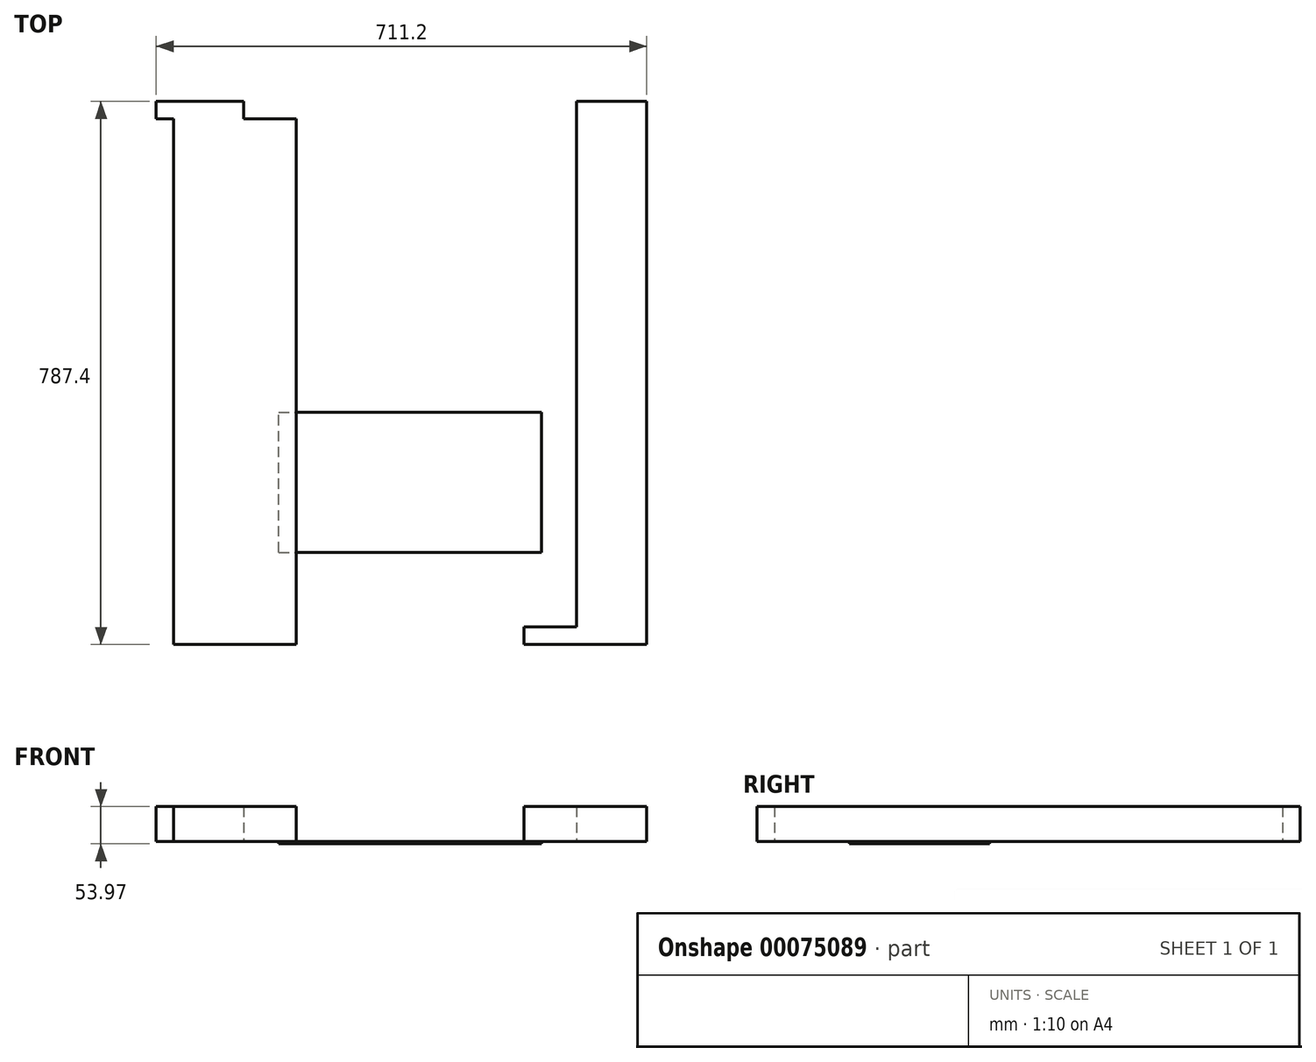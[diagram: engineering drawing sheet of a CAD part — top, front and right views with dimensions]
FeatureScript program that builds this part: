
annotation { "Feature Type Name" : "Feature", "Feature Type Description" : "" }
export const myFeature = defineFeature(function(context is Context, id is Id, definition is map)
    precondition{}
    {
        {
            var Q0;
            Q0=qCreatedBy(makeId("Top.planeOp"),FACE);
            var sketch = newSketch(context, id + "F0", { "sketchPlane" : qUnion([Q0])});
            skLineSegment(sketch, "E0.right", {"start": v(-494.41, 506.03) * mm, "end": v(-494.41, -281.37) * mm});
            skLineSegment(sketch, "E1.right", {"start": v(-596.01, 506.03) * mm, "end": v(-596.01, -281.37) * mm});
            skLineSegment(sketch, "E2.bottom", {"start": v(-621.41, 506.03) * mm, "end": v(115.19, 506.03) * mm});
            skLineSegment(sketch, "E2.top", {"start": v(-621.41, -281.37) * mm, "end": v(115.19, -281.37) * mm});
            skLineSegment(sketch, "E3.right", {"start": v(89.79, 506.03) * mm, "end": v(89.79, -281.37) * mm});
            skLineSegment(sketch, "E4.left", {"start": v(-11.81, 506.03) * mm, "end": v(-11.81, -281.37) * mm});
            skLineSegment(sketch, "E4.right", {"start": v(13.59, 506.03) * mm, "end": v(13.59, -281.37) * mm});
            skLineSegment(sketch, "E5.bottom", {"start": v(-621.41, -281.37) * mm, "end": v(-418.21, -281.37) * mm});
            skLineSegment(sketch, "E6.bottom", {"start": v(115.19, -281.37) * mm, "end": v(-88.01, -281.37) * mm});
            skLineSegment(sketch, "E5.top", {"start": v(-621.41, -255.97) * mm, "end": v(-418.21, -255.97) * mm});
            skLineSegment(sketch, "E6.top", {"start": v(115.19, -255.97) * mm, "end": v(-88.01, -255.97) * mm});
            skLineSegment(sketch, "E0.left", {"start": v(-519.81, 506.03) * mm, "end": v(-519.81, -281.37) * mm});
            skLineSegment(sketch, "E6.left", {"start": v(115.19, -281.37) * mm, "end": v(115.19, -255.97) * mm});
            skLineSegment(sketch, "E1.top", {"start": v(-621.41, -281.37) * mm, "end": v(-596.01, -281.37) * mm});
            skLineSegment(sketch, "E3.bottom", {"start": v(115.19, 506.03) * mm, "end": v(89.79, 506.03) * mm});
            skLineSegment(sketch, "E3.top", {"start": v(115.19, -281.37) * mm, "end": v(89.79, -281.37) * mm});
            skLineSegment(sketch, "E4.bottom", {"start": v(-11.81, 506.03) * mm, "end": v(13.59, 506.03) * mm});
            skLineSegment(sketch, "E4.top", {"start": v(-11.81, -281.37) * mm, "end": v(13.59, -281.37) * mm});
            skLineSegment(sketch, "E1.bottom", {"start": v(-621.41, 506.03) * mm, "end": v(-596.01, 506.03) * mm});
            skLineSegment(sketch, "E6.right", {"start": v(-88.01, -281.37) * mm, "end": v(-88.01, -255.97) * mm});
            skLineSegment(sketch, "E5.right", {"start": v(-418.21, -281.37) * mm, "end": v(-418.21, -255.97) * mm});
            skLineSegment(sketch, "E0.bottom", {"start": v(-519.81, 506.03) * mm, "end": v(-494.41, 506.03) * mm});
            skLineSegment(sketch, "E0.top", {"start": v(-519.81, -281.37) * mm, "end": v(-494.41, -281.37) * mm});
            skLineSegment(sketch, "E5.left", {"start": v(-621.41, -281.37) * mm, "end": v(-621.41, -255.97) * mm});
            skLineSegment(sketch, "E7.top", {"start": v(-621.41, 480.63) * mm, "end": v(115.19, 480.63) * mm});
            skLineSegment(sketch, "E7.left", {"start": v(-621.41, 506.03) * mm, "end": v(-621.41, 480.63) * mm});
            skLineSegment(sketch, "E7.right", {"start": v(115.19, 506.03) * mm, "end": v(115.19, 480.63) * mm});
            skLineSegment(sketch, "E8.bottom", {"start": v(-418.21, -255.97) * mm, "end": v(-443.61, -255.97) * mm});
            skLineSegment(sketch, "E8.top", {"start": v(-418.21, 480.63) * mm, "end": v(-443.61, 480.63) * mm});
            skLineSegment(sketch, "E8.left", {"start": v(-418.21, -255.97) * mm, "end": v(-418.21, 480.63) * mm});
            skLineSegment(sketch, "E8.right", {"start": v(-443.61, -255.97) * mm, "end": v(-443.61, 480.63) * mm});
            skLineSegment(sketch, "E9.bottom", {"start": v(-88.01, -255.97) * mm, "end": v(-62.61, -255.97) * mm});
            skLineSegment(sketch, "E9.top", {"start": v(-88.01, 480.63) * mm, "end": v(-62.61, 480.63) * mm});
            skLineSegment(sketch, "E9.left", {"start": v(-88.01, -255.97) * mm, "end": v(-88.01, 480.63) * mm});
            skLineSegment(sketch, "E9.right", {"start": v(-62.61, -255.97) * mm, "end": v(-62.61, 480.63) * mm});
            skSolve(sketch);
        }
        {
            var Q0;
            {var subQ5=sQuery(id+"F0.wireOp",EDGE,"E2.left");Q0=makeQuery(id+"F0.imprint","IMPRINT",FACE,{"disambiguationData":[TD([[makeQuery(id+"F0.imprint","IMPRINT",EDGE,{"derivedFrom":subQ5}),1.0]])]});}
            var Q1;
            {var subQ5=sQuery(id+"F0.wireOp",EDGE,"E7.left");Q1=makeQuery(id+"F0.imprint","IMPRINT",FACE,{"disambiguationData":[TD([[makeQuery(id+"F0.imprint","IMPRINT",EDGE,{"derivedFrom":subQ5}),1.0]])]});}
            var Q2;
            {var subQ0=sQuery(id+"F0.wireOp",EDGE,"E2.bottom");var subQ1=sQuery(id+"F0.wireOp",EDGE,"E1.right");var subQ2=makeQuery(id+"F0.imprint","INTERSECT",VERTEX,{"derivedFrom":[subQ1,subQ0]});Q2=makeQuery(id+"F0.imprint","IMPRINT",FACE,{"disambiguationData":[TD([[makeQuery(id+"F0.imprint","IMPRINT",EDGE,{"disambiguationData":[TD([[subQ2,-1.0]])],"derivedFrom":subQ1}),1.0]])]});}
            var Q3;
            {var subQ0=sQuery(id+"F0.wireOp",EDGE,"E2.bottom");var subQ1=sQuery(id+"F0.wireOp",EDGE,"E0.right");var subQ2=makeQuery(id+"F0.imprint","INTERSECT",VERTEX,{"derivedFrom":[subQ1,subQ0]});Q3=makeQuery(id+"F0.imprint","IMPRINT",FACE,{"disambiguationData":[TD([[makeQuery(id+"F0.imprint","IMPRINT",EDGE,{"disambiguationData":[TD([[subQ2,-1.0]])],"derivedFrom":subQ1}),-1.0]])]});}
            var Q4;
            {var subQ0=sQuery(id+"F0.wireOp",EDGE,"E7.top");var subQ1=sQuery(id+"F0.wireOp",EDGE,"E0.right");var subQ2=makeQuery(id+"F0.imprint","INTERSECT",VERTEX,{"derivedFrom":[subQ1,subQ0]});Q4=makeQuery(id+"F0.imprint","IMPRINT",FACE,{"disambiguationData":[TD([[makeQuery(id+"F0.imprint","IMPRINT",EDGE,{"disambiguationData":[TD([[subQ2,-1.0]])],"derivedFrom":subQ1}),-1.0]])]});}
            var Q5;
            {var subQ0=sQuery(id+"F0.wireOp",EDGE,"E1.top");Q5=makeQuery(id+"F0.imprint","IMPRINT",FACE,{"disambiguationData":[TD([[makeQuery(id+"F0.imprint","IMPRINT",EDGE,{"derivedFrom":subQ0}),1.0]])]});}
            var Q6;
            {var subQ1=sQuery(id+"F0.wireOp",EDGE,"E1.right");var subQ3=sQuery(id+"F0.wireOp",EDGE,"E5.top");var subQ4=makeQuery(id+"F0.imprint","INTERSECT",VERTEX,{"derivedFrom":[subQ1,subQ3]});Q6=makeQuery(id+"F0.imprint","IMPRINT",FACE,{"disambiguationData":[TD([[makeQuery(id+"F0.imprint","IMPRINT",EDGE,{"disambiguationData":[TD([[subQ4,-1.0]])],"derivedFrom":subQ3}),-1.0]])]});}
            var Q7;
            {var subQ0=sQuery(id+"F0.wireOp",EDGE,"E0.top");Q7=makeQuery(id+"F0.imprint","IMPRINT",FACE,{"disambiguationData":[TD([[makeQuery(id+"F0.imprint","IMPRINT",EDGE,{"derivedFrom":subQ0}),1.0]])]});}
            var Q8;
            {var subQ5=sQuery(id+"F0.wireOp",EDGE,"E5.right");Q8=makeQuery(id+"F0.imprint","IMPRINT",FACE,{"disambiguationData":[TD([[makeQuery(id+"F0.imprint","IMPRINT",EDGE,{"derivedFrom":subQ5}),1.0]])]});}
            var Q9;
            {var subQ5=sQuery(id+"F0.wireOp",EDGE,"E6.right");Q9=makeQuery(id+"F0.imprint","IMPRINT",FACE,{"disambiguationData":[TD([[makeQuery(id+"F0.imprint","IMPRINT",EDGE,{"derivedFrom":subQ5}),-1.0]])]});}
            var Q10;
            {var subQ0=sQuery(id+"F0.wireOp",EDGE,"E4.top");Q10=makeQuery(id+"F0.imprint","IMPRINT",FACE,{"disambiguationData":[TD([[makeQuery(id+"F0.imprint","IMPRINT",EDGE,{"derivedFrom":subQ0}),1.0]])]});}
            var Q11;
            {var subQ0=sQuery(id+"F0.wireOp",EDGE,"E7.top");var subQ1=sQuery(id+"F0.wireOp",EDGE,"E4.left");var subQ2=makeQuery(id+"F0.imprint","INTERSECT",VERTEX,{"derivedFrom":[subQ1,subQ0]});Q11=makeQuery(id+"F0.imprint","IMPRINT",FACE,{"disambiguationData":[TD([[makeQuery(id+"F0.imprint","IMPRINT",EDGE,{"disambiguationData":[TD([[subQ2,-1.0]])],"derivedFrom":subQ1}),1.0]])]});}
            var Q12;
            {var subQ1=sQuery(id+"F0.wireOp",EDGE,"E3.right");var subQ3=sQuery(id+"F0.wireOp",EDGE,"E6.top");var subQ4=makeQuery(id+"F0.imprint","INTERSECT",VERTEX,{"derivedFrom":[subQ1,subQ3]});Q12=makeQuery(id+"F0.imprint","IMPRINT",FACE,{"disambiguationData":[TD([[makeQuery(id+"F0.imprint","IMPRINT",EDGE,{"disambiguationData":[TD([[subQ4,-1.0]])],"derivedFrom":subQ3}),1.0]])]});}
            var Q13;
            {var subQ4=sQuery(id+"F0.wireOp",EDGE,"E6.left");Q13=makeQuery(id+"F0.imprint","IMPRINT",FACE,{"disambiguationData":[TD([[makeQuery(id+"F0.imprint","IMPRINT",EDGE,{"derivedFrom":subQ4}),1.0]])]});}
            var Q14;
            {var subQ5=sQuery(id+"F0.wireOp",EDGE,"E3.left");Q14=makeQuery(id+"F0.imprint","IMPRINT",FACE,{"disambiguationData":[TD([[makeQuery(id+"F0.imprint","IMPRINT",EDGE,{"derivedFrom":subQ5}),-1.0]])]});}
            var Q15;
            {var subQ0=sQuery(id+"F0.wireOp",EDGE,"E2.bottom");var subQ1=sQuery(id+"F0.wireOp",EDGE,"E0.right");var subQ2=makeQuery(id+"F0.imprint","INTERSECT",VERTEX,{"derivedFrom":[subQ1,subQ0]});Q15=makeQuery(id+"F0.imprint","IMPRINT",FACE,{"disambiguationData":[TD([[makeQuery(id+"F0.imprint","IMPRINT",EDGE,{"disambiguationData":[TD([[subQ2,-1.0]])],"derivedFrom":subQ1}),1.0]])]});}
            var Q16;
            {var subQ0=sQuery(id+"F0.wireOp",EDGE,"E2.bottom");var subQ1=sQuery(id+"F0.wireOp",EDGE,"E4.left");var subQ2=makeQuery(id+"F0.imprint","INTERSECT",VERTEX,{"derivedFrom":[subQ1,subQ0]});Q16=makeQuery(id+"F0.imprint","IMPRINT",FACE,{"disambiguationData":[TD([[makeQuery(id+"F0.imprint","IMPRINT",EDGE,{"disambiguationData":[TD([[subQ2,-1.0]])],"derivedFrom":subQ1}),1.0]])]});}
            var Q17;
            {var subQ0=sQuery(id+"F0.wireOp",EDGE,"E2.bottom");var subQ1=sQuery(id+"F0.wireOp",EDGE,"E3.right");var subQ2=makeQuery(id+"F0.imprint","INTERSECT",VERTEX,{"derivedFrom":[subQ1,subQ0]});Q17=makeQuery(id+"F0.imprint","IMPRINT",FACE,{"disambiguationData":[TD([[makeQuery(id+"F0.imprint","IMPRINT",EDGE,{"disambiguationData":[TD([[subQ2,-1.0]])],"derivedFrom":subQ1}),-1.0]])]});}
            var Q18;
            {var subQ5=sQuery(id+"F0.wireOp",EDGE,"E7.right");Q18=makeQuery(id+"F0.imprint","IMPRINT",FACE,{"disambiguationData":[TD([[makeQuery(id+"F0.imprint","IMPRINT",EDGE,{"derivedFrom":subQ5}),-1.0]])]});}
            extrude(context, id + "F1", {"entities" : qUnion([Q0, Q1, Q2, Q3, Q4, Q5, Q6, Q7, Q8, Q9, Q10, Q11, Q12, Q13, Q14, Q15, Q16, Q17, Q18]), "depth" : 50.8 * mm});
        }
        {
            var Q0;
            Q0=makeQuery(id+"F1.opExtrude","CAP_FACE",FACE,{"disambiguationData":[OSD([sQuery(id+"F0.wireOp",EDGE,"E0.right"),sQuery(id+"F0.wireOp",EDGE,"E1.right"),sQuery(id+"F0.wireOp",EDGE,"E3.right"),sQuery(id+"F0.wireOp",EDGE,"E4.left"),sQuery(id+"F0.wireOp",EDGE,"E4.right"),sQuery(id+"F0.wireOp",EDGE,"E5.bottom"),sQuery(id+"F0.wireOp",EDGE,"E6.bottom"),sQuery(id+"F0.wireOp",EDGE,"E5.top"),sQuery(id+"F0.wireOp",EDGE,"E6.top"),sQuery(id+"F0.wireOp",EDGE,"E0.left"),sQuery(id+"F0.wireOp",EDGE,"E2.left"),sQuery(id+"F0.wireOp",EDGE,"E3.left"),sQuery(id+"F0.wireOp",EDGE,"E6.left"),sQuery(id+"F0.wireOp",EDGE,"E1.top"),sQuery(id+"F0.wireOp",EDGE,"E3.top"),sQuery(id+"F0.wireOp",EDGE,"E4.top"),sQuery(id+"F0.wireOp",EDGE,"E6.right"),sQuery(id+"F0.wireOp",EDGE,"E5.right"),sQuery(id+"F0.wireOp",EDGE,"E0.top"),sQuery(id+"F0.wireOp",EDGE,"E5.left"),sQuery(id+"F0.wireOp",EDGE,"E2.bottom"),sQuery(id+"F0.wireOp",EDGE,"E7.top"),sQuery(id+"F0.wireOp",EDGE,"E7.left"),sQuery(id+"F0.wireOp",EDGE,"E7.right"),sQuery(id+"F0.wireOp",EDGE,"E8.bottom"),sQuery(id+"F0.wireOp",EDGE,"E8.top"),sQuery(id+"F0.wireOp",EDGE,"E9.bottom"),sQuery(id+"F0.wireOp",EDGE,"E9.top")])],"isStart":false});
            var sketch = newSketch(context, id + "F2", { "sketchPlane" : qUnion([Q0])});
            skLineSegment(sketch, "E10.bottom", {"start": v(-62.61, 480.63) * mm, "end": v(-88.01, 480.63) * mm});
            skLineSegment(sketch, "E10.top", {"start": v(-62.61, -255.97) * mm, "end": v(-88.01, -255.97) * mm});
            skLineSegment(sketch, "E10.left", {"start": v(-62.61, 480.63) * mm, "end": v(-62.61, -255.97) * mm});
            skLineSegment(sketch, "E10.right", {"start": v(-88.01, 480.63) * mm, "end": v(-88.01, -255.97) * mm});
            skLineSegment(sketch, "E11.bottom", {"start": v(-418.21, -255.97) * mm, "end": v(-443.61, -255.97) * mm});
            skLineSegment(sketch, "E11.top", {"start": v(-418.21, 480.63) * mm, "end": v(-443.61, 480.63) * mm});
            skLineSegment(sketch, "E11.left", {"start": v(-418.21, -255.97) * mm, "end": v(-418.21, 480.63) * mm});
            skLineSegment(sketch, "E11.right", {"start": v(-443.61, -255.97) * mm, "end": v(-443.61, 480.63) * mm});
            skSolve(sketch);
        }
        {
            var Q0;
            Q0=makeQuery(id+"F2.imprint","IMPRINT",FACE,{"disambiguationData":[TD([[makeQuery(id+"F2.imprint","IMPRINT",EDGE,{"derivedFrom":sQuery(id+"F2.wireOp",EDGE,"E11.bottom")}),1.0]])]});
            var Q1;
            Q1=makeQuery(id+"F2.imprint","IMPRINT",FACE,{"disambiguationData":[TD([[makeQuery(id+"F2.imprint","IMPRINT",EDGE,{"derivedFrom":sQuery(id+"F2.wireOp",EDGE,"E10.bottom")}),-1.0]])]});
            extrude(context, id + "F3", {"entities" : qUnion([Q0, Q1]), "operationType" : NewBodyOperationType.ADD, "oppositeDirection" : true, "depth" : 50.8 * mm});
        }
        {
            var Q0;
            Q0=makeQuery(id+"F3.boolean.opBoolean","MERGE",FACE,{"derivedFrom":[makeQuery(id+"F1.opExtrude","CAP_FACE",FACE,{"disambiguationData":[OSD([sQuery(id+"F0.wireOp",EDGE,"E0.right"),sQuery(id+"F0.wireOp",EDGE,"E1.right"),sQuery(id+"F0.wireOp",EDGE,"E3.right"),sQuery(id+"F0.wireOp",EDGE,"E4.left"),sQuery(id+"F0.wireOp",EDGE,"E4.right"),sQuery(id+"F0.wireOp",EDGE,"E5.bottom"),sQuery(id+"F0.wireOp",EDGE,"E6.bottom"),sQuery(id+"F0.wireOp",EDGE,"E5.top"),sQuery(id+"F0.wireOp",EDGE,"E6.top"),sQuery(id+"F0.wireOp",EDGE,"E0.left"),sQuery(id+"F0.wireOp",EDGE,"E2.left"),sQuery(id+"F0.wireOp",EDGE,"E3.left"),sQuery(id+"F0.wireOp",EDGE,"E6.left"),sQuery(id+"F0.wireOp",EDGE,"E1.top"),sQuery(id+"F0.wireOp",EDGE,"E3.top"),sQuery(id+"F0.wireOp",EDGE,"E4.top"),sQuery(id+"F0.wireOp",EDGE,"E6.right"),sQuery(id+"F0.wireOp",EDGE,"E5.right"),sQuery(id+"F0.wireOp",EDGE,"E0.top"),sQuery(id+"F0.wireOp",EDGE,"E5.left"),sQuery(id+"F0.wireOp",EDGE,"E2.bottom"),sQuery(id+"F0.wireOp",EDGE,"E7.top"),sQuery(id+"F0.wireOp",EDGE,"E7.left"),sQuery(id+"F0.wireOp",EDGE,"E7.right"),sQuery(id+"F0.wireOp",EDGE,"E8.bottom"),sQuery(id+"F0.wireOp",EDGE,"E8.top"),sQuery(id+"F0.wireOp",EDGE,"E9.bottom"),sQuery(id+"F0.wireOp",EDGE,"E9.top")])],"isStart":true}),makeQuery(id+"F3.opExtrude","CAP_FACE",FACE,{"disambiguationData":[OSD([sQuery(id+"F2.wireOp",EDGE,"E10.bottom"),sQuery(id+"F2.wireOp",EDGE,"E10.top"),sQuery(id+"F2.wireOp",EDGE,"E10.left"),sQuery(id+"F2.wireOp",EDGE,"E10.right")])],"isStart":false}),makeQuery(id+"F3.opExtrude","CAP_FACE",FACE,{"disambiguationData":[OSD([sQuery(id+"F2.wireOp",EDGE,"E11.bottom"),sQuery(id+"F2.wireOp",EDGE,"E11.top"),sQuery(id+"F2.wireOp",EDGE,"E11.left"),sQuery(id+"F2.wireOp",EDGE,"E11.right")])],"isStart":false})]});
            var sketch = newSketch(context, id + "F4", { "sketchPlane" : qUnion([Q0])});
            skLineSegment(sketch, "E12.bottom", {"start": v(-443.61, 147.64) * mm, "end": v(-62.61, 147.64) * mm});
            skLineSegment(sketch, "E12.top", {"start": v(-443.61, -55.56) * mm, "end": v(-62.61, -55.56) * mm});
            skLineSegment(sketch, "E12.left", {"start": v(-443.61, 147.64) * mm, "end": v(-443.61, -55.56) * mm});
            skLineSegment(sketch, "E12.right", {"start": v(-62.61, 147.64) * mm, "end": v(-62.61, -55.56) * mm});
            skSolve(sketch);
        }
        {
            var Q0;
            {var subQ0=sQuery(id+"F4.wireOp",EDGE,"E12.bottom");var subQ1=makeQuery(id+"F3.boolean.opBoolean","MERGE",EDGE,{"derivedFrom":[makeQuery(id+"F1.opExtrude","CAP_EDGE",EDGE,{"disambiguationData":[OSD([sQuery(id+"F0.wireOp",EDGE,"E5.right")])],"isStart":true}),makeQuery(id+"F3.opExtrude","CAP_EDGE",EDGE,{"disambiguationData":[OSD([sQuery(id+"F2.wireOp",EDGE,"E11.left")])],"isStart":false})]});var subQ2=makeQuery(id+"F4.imprint","INTERSECT",VERTEX,{"derivedFrom":[subQ1,subQ0]});Q0=makeQuery(id+"F4.imprint","IMPRINT",FACE,{"disambiguationData":[TD([[makeQuery(id+"F4.imprint","IMPRINT",EDGE,{"disambiguationData":[TD([[subQ2,-1.0]])],"derivedFrom":subQ0}),-1.0]])]});}
            var Q1;
            {var subQ0=sQuery(id+"F4.wireOp",EDGE,"E12.left");Q1=makeQuery(id+"F4.imprint","IMPRINT",FACE,{"disambiguationData":[TD([[makeQuery(id+"F4.imprint","IMPRINT",EDGE,{"derivedFrom":subQ0}),1.0]])]});}
            var Q2;
            {var subQ0=sQuery(id+"F4.wireOp",EDGE,"E12.right");Q2=makeQuery(id+"F4.imprint","IMPRINT",FACE,{"disambiguationData":[TD([[makeQuery(id+"F4.imprint","IMPRINT",EDGE,{"derivedFrom":subQ0}),1.0]])]});}
            extrude(context, id + "F5", {"entities" : qUnion([Q0, Q1, Q2]), "operationType" : NewBodyOperationType.ADD, "depth" : 3.17 * mm});
        }
    });
